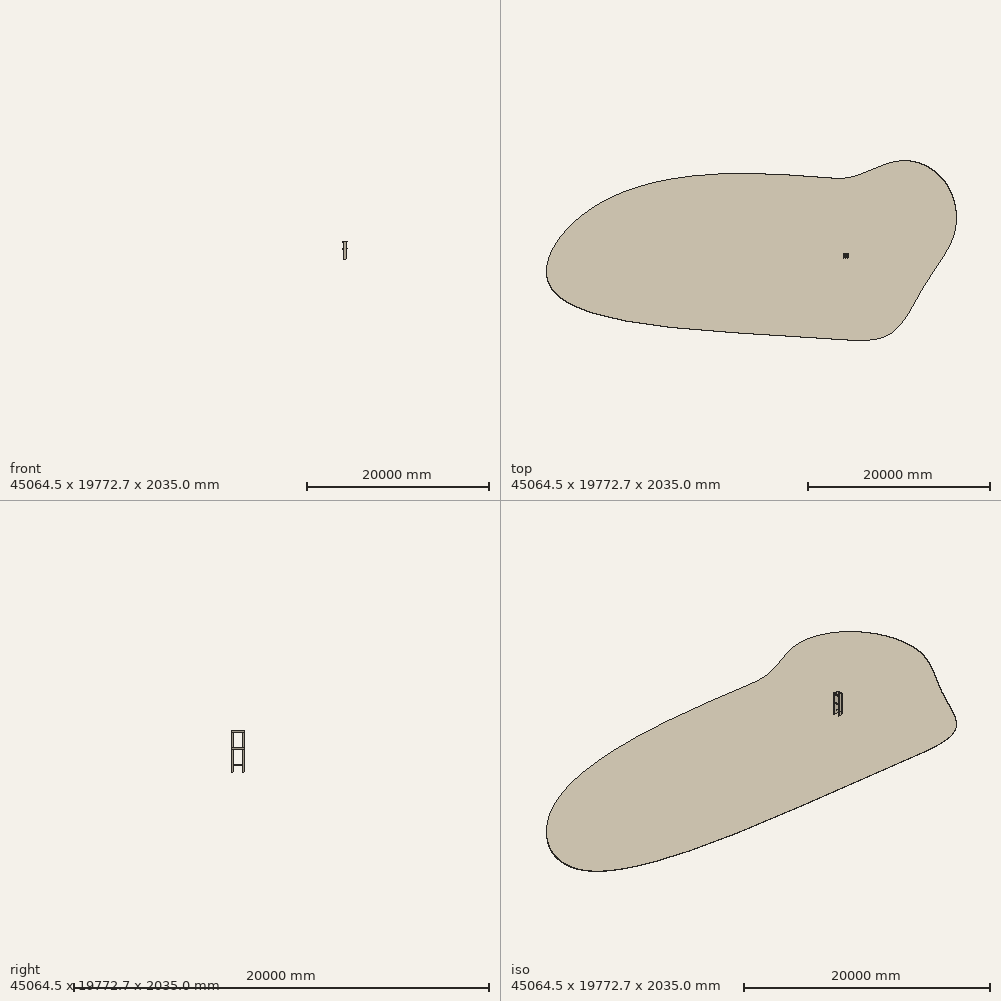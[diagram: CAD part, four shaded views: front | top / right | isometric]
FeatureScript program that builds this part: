
annotation { "Feature Type Name" : "Feature", "Feature Type Description" : "" }
export const myFeature = defineFeature(function(context is Context, id is Id, definition is map)
    precondition{}
    {
        {
            var Q0;
            Q0=qCreatedBy(makeId("Top.planeOp"),FACE);
            var sketch = newSketch(context, id + "F0", { "sketchPlane" : qUnion([Q0])});
            skLineSegment(sketch, "E0", {"start": v(-200, -312.5) * mm, "end": v(-200, -202.5) * mm});
            skLineSegment(sketch, "E1", {"start": v(-200, -202.5) * mm, "end": v(200, -202.5) * mm});
            skLineSegment(sketch, "E2", {"start": v(200, -202.5) * mm, "end": v(200, -312.5) * mm});
            skLineSegment(sketch, "E3", {"start": v(200, -312.5) * mm, "end": v(185, -312.5) * mm});
            skLineSegment(sketch, "E4", {"start": v(185, -312.5) * mm, "end": v(185, -217.5) * mm});
            skLineSegment(sketch, "E5", {"start": v(185, -217.5) * mm, "end": v(-185, -217.5) * mm});
            skLineSegment(sketch, "E6", {"start": v(-185, -217.5) * mm, "end": v(-185, -312.5) * mm});
            skLineSegment(sketch, "E7", {"start": v(-185, -312.5) * mm, "end": v(-200, -312.5) * mm});
            skLineSegment(sketch, "E8.MirrorCS", {"start": v(-200, 312.5) * mm, "end": v(-200, 202.5) * mm});
            skLineSegment(sketch, "E9.MirrorCS", {"start": v(-200, 202.5) * mm, "end": v(200, 202.5) * mm});
            skLineSegment(sketch, "E10.MirrorCS", {"start": v(185, 217.5) * mm, "end": v(-185, 217.5) * mm});
            skLineSegment(sketch, "E11.MirrorCS", {"start": v(185, 312.5) * mm, "end": v(185, 217.5) * mm});
            skLineSegment(sketch, "E12.MirrorCS", {"start": v(-185, 217.5) * mm, "end": v(-185, 312.5) * mm});
            skLineSegment(sketch, "E13.MirrorCS", {"start": v(200, 202.5) * mm, "end": v(200, 312.5) * mm});
            skLineSegment(sketch, "E14.MirrorCS", {"start": v(-185, 312.5) * mm, "end": v(-200, 312.5) * mm});
            skLineSegment(sketch, "E15.MirrorCS", {"start": v(200, 312.5) * mm, "end": v(185, 312.5) * mm});
            skSolve(sketch);
        }
        {
            var Q0;
            Q0 = qSketchRegion(id + "F0", true);
            extrude(context, id + "F1", {"entities" : qUnion([Q0]), "depth" : 2010 * mm, "offsetDistance" : 25 * mm});
        }
        {
            var Q0;
            Q0=makeQuery(id+"F1.opExtrude","SWEPT_FACE",FACE,{"disambiguationData":[OSD([sQuery(id+"F0.wireOp",EDGE,"E5")])]});
            var sketch = newSketch(context, id + "F2", { "sketchPlane" : qUnion([Q0])});
            skCircle(sketch, "E16", {"center": v(0, 355) * mm, "radius": 19 * mm});
            skSolve(sketch);
        }
        {
            var Q0;
            Q0=makeQuery(id+"F2.imprint","IMPRINT",FACE,{"disambiguationData":[TD([[makeQuery(id+"F2.imprint","IMPRINT",EDGE,{"derivedFrom":sQuery(id+"F2.wireOp",EDGE,"E16")}),1.0]])]});
            extrude(context, id + "F3", {"entities" : qUnion([Q0]), "operationType" : NewBodyOperationType.REMOVE, "endBound" : BoundingType.THROUGH_ALL, "oppositeDirection" : true, "depth" : 25 * mm, "offsetDistance" : 25 * mm});
        }
        {
            var Q0;
            Q0=qCreatedBy(makeId("Right.planeOp"),FACE);
            var sketch = newSketch(context, id + "F4", { "sketchPlane" : qUnion([Q0])});
            skCircle(sketch, "E17", {"center": v(-257.5, 1098) * mm, "radius": 7.5 * mm});
            skCircle(sketch, "E18", {"center": v(257.5, 1098) * mm, "radius": 7.5 * mm});
            skCircle(sketch, "E19", {"center": v(-257.5, 1978) * mm, "radius": 7.5 * mm});
            skCircle(sketch, "E20", {"center": v(257.5, 1978) * mm, "radius": 7.5 * mm});
            skCircle(sketch, "E21", {"center": v(257.5, 1937) * mm, "radius": 7.5 * mm});
            skCircle(sketch, "E22", {"center": v(-257.5, 1937) * mm, "radius": 7.5 * mm});
            skCircle(sketch, "E23", {"center": v(257.5, 1158) * mm, "radius": 7.5 * mm});
            skCircle(sketch, "E24", {"center": v(-257.5, 1158) * mm, "radius": 7.5 * mm});
            skSolve(sketch);
        }
        {
            var Q0;
            Q0 = qSketchRegion(id + "F4", true);
            extrude(context, id + "F5", {"entities" : qUnion([Q0]), "operationType" : NewBodyOperationType.REMOVE, "endBound" : BoundingType.THROUGH_ALL, "oppositeDirection" : true, "depth" : 25 * mm, "offsetDistance" : 25 * mm, "hasSecondDirection" : true, "secondDirectionBound" : SecondDirectionBoundingType.THROUGH_ALL, "secondDirectionOppositeDirection" : false, "secondDirectionDepth" : 25 * mm});
        }
        {
            var Q0;
            Q0=qCreatedBy(makeId("Top.planeOp"),FACE);
            var sketch = newSketch(context, id + "F6", { "sketchPlane" : qUnion([Q0])});
            skFitSpline(sketch, "E25", {"points": [v(-26060.01, 6307.68) * mm, v(-4444.75, 8762.1) * mm, v(1029.42, 8782.8) * mm, v(6125.61, 10472.14) * mm, v(10723.74, 8341.28) * mm, v(11981.11, 2728.24) * mm, v(8613.99, -3299.12) * mm, v(5082.12, -8449.76) * mm, v(-4741.28, -8891.89) * mm, v(-32336.68, -3635.44) * mm, v(-26060.01, 6307.68) * mm]});
            skSolve(sketch);
        }
        {
            var Q0;
            Q0=makeQuery(id+"F6.imprint","IMPRINT",FACE,{"disambiguationData":[TD([[makeQuery(id+"F6.imprint","IMPRINT",EDGE,{"derivedFrom":sQuery(id+"F6.wireOp",EDGE,"E25")}),-1.0]])]});
            extrude(context, id + "F7", {"entities" : qUnion([Q0]), "oppositeDirection" : true, "depth" : 25 * mm, "offsetDistance" : 25 * mm});
        }
        {
            var Q0;
            Q0=makeQuery(id+"F1.opExtrude","SWEPT_FACE",FACE,{"disambiguationData":[OSD([sQuery(id+"F0.wireOp",EDGE,"E0")])]});
            var sketch = newSketch(context, id + "F8", { "sketchPlane" : qUnion([Q0])});
            skLineSegment(sketch, "E26.bottom", {"start": v(-300, 1178) * mm, "end": v(300, 1178) * mm});
            skLineSegment(sketch, "E26.top", {"start": v(-300, 1078) * mm, "end": v(300, 1078) * mm});
            skLineSegment(sketch, "E26.left", {"start": v(-300, 1178) * mm, "end": v(-300, 1078) * mm});
            skLineSegment(sketch, "E26.right", {"start": v(300, 1178) * mm, "end": v(300, 1078) * mm});
            skLineSegment(sketch, "E27", {"start": v(-300, 1128) * mm, "end": v(300, 1128) * mm});
            skLineSegment(sketch, "E28.bottom", {"start": v(-300, 2007.5) * mm, "end": v(300, 2007.5) * mm});
            skLineSegment(sketch, "E28.top", {"start": v(-300, 1907.5) * mm, "end": v(300, 1907.5) * mm});
            skLineSegment(sketch, "E28.left", {"start": v(-300, 2007.5) * mm, "end": v(-300, 1907.5) * mm});
            skLineSegment(sketch, "E28.right", {"start": v(300, 2007.5) * mm, "end": v(300, 1907.5) * mm});
            skLineSegment(sketch, "E29", {"start": v(-300, 1957.5) * mm, "end": v(300, 1957.5) * mm});
            skCircle(sketch, "E30.0", {"center": v(-257.5, 1978) * mm, "radius": 7.5 * mm});
            skCircle(sketch, "E31.0", {"center": v(-257.5, 1937) * mm, "radius": 7.5 * mm});
            skCircle(sketch, "E32.0", {"center": v(257.5, 1978) * mm, "radius": 7.5 * mm});
            skCircle(sketch, "E33.0", {"center": v(257.5, 1937) * mm, "radius": 7.5 * mm});
            skCircle(sketch, "E34.0", {"center": v(257.5, 1158) * mm, "radius": 7.5 * mm});
            skCircle(sketch, "E35.0", {"center": v(257.5, 1098) * mm, "radius": 7.5 * mm});
            skCircle(sketch, "E36.0", {"center": v(-257.5, 1098) * mm, "radius": 7.5 * mm});
            skCircle(sketch, "E37.0", {"center": v(-257.5, 1158) * mm, "radius": 7.5 * mm});
            skSolve(sketch);
        }
        {
            var Q0;
            {var subQ6=sQuery(id+"F8.wireOp",EDGE,"E28.bottom");Q0=makeQuery(id+"F8.imprint","IMPRINT",FACE,{"disambiguationData":[TD([[makeQuery(id+"F8.imprint","IMPRINT",EDGE,{"derivedFrom":subQ6}),-1.0]])]});}
            var Q1;
            Q1=makeQuery(id+"F8.imprint","IMPRINT",FACE,{"disambiguationData":[TD([[makeQuery(id+"F8.imprint","IMPRINT",EDGE,{"derivedFrom":sQuery(id+"F8.wireOp",EDGE,"E31.0")}),-1.0]])]});
            var Q2;
            Q2=makeQuery(id+"F8.imprint","IMPRINT",FACE,{"disambiguationData":[TD([[makeQuery(id+"F8.imprint","IMPRINT",EDGE,{"derivedFrom":sQuery(id+"F8.wireOp",EDGE,"E37.0")}),-1.0]])]});
            var Q3;
            Q3=makeQuery(id+"F8.imprint","IMPRINT",FACE,{"disambiguationData":[TD([[makeQuery(id+"F8.imprint","IMPRINT",EDGE,{"derivedFrom":sQuery(id+"F8.wireOp",EDGE,"E36.0")}),-1.0]])]});
            var Q4;
            Q4=makeQuery(id+"F8.imprint","IMPRINT",FACE,{"disambiguationData":[TD([[makeQuery(id+"F8.imprint","IMPRINT",EDGE,{"derivedFrom":sQuery(id+"F8.wireOp",EDGE,"E34.0")}),-1.0]])]});
            var Q5;
            Q5=makeQuery(id+"F8.imprint","IMPRINT",FACE,{"disambiguationData":[TD([[makeQuery(id+"F8.imprint","IMPRINT",EDGE,{"derivedFrom":sQuery(id+"F8.wireOp",EDGE,"E35.0")}),-1.0]])]});
            var Q6;
            Q6=makeQuery(id+"F8.imprint","IMPRINT",FACE,{"disambiguationData":[TD([[makeQuery(id+"F8.imprint","IMPRINT",EDGE,{"derivedFrom":sQuery(id+"F8.wireOp",EDGE,"E32.0")}),-1.0]])]});
            var Q7;
            Q7=makeQuery(id+"F8.imprint","IMPRINT",FACE,{"disambiguationData":[TD([[makeQuery(id+"F8.imprint","IMPRINT",EDGE,{"derivedFrom":sQuery(id+"F8.wireOp",EDGE,"E33.0")}),-1.0]])]});
            extrude(context, id + "F9", {"entities" : qUnion([Q0, Q1, Q2, Q3, Q4, Q5, Q6, Q7]), "depth" : 25 * mm, "offsetDistance" : 25 * mm});
        }
        {
            var Q0;
            Q0=makeQuery(id+"F9.opExtrude","SWEPT_BODY",BODY,{"disambiguationData":[OSD([sQuery(id+"F8.wireOp",EDGE,"E28.bottom"),sQuery(id+"F8.wireOp",EDGE,"E28.top"),sQuery(id+"F8.wireOp",EDGE,"E28.left"),sQuery(id+"F8.wireOp",EDGE,"E28.right"),sQuery(id+"F8.wireOp",EDGE,"E30.0"),sQuery(id+"F8.wireOp",EDGE,"E31.0"),sQuery(id+"F8.wireOp",EDGE,"E32.0"),sQuery(id+"F8.wireOp",EDGE,"E33.0")])]});
            var Q1;
            Q1=makeQuery(id+"F9.opExtrude","SWEPT_BODY",BODY,{"disambiguationData":[OSD([sQuery(id+"F8.wireOp",EDGE,"E26.bottom"),sQuery(id+"F8.wireOp",EDGE,"E26.top"),sQuery(id+"F8.wireOp",EDGE,"E26.left"),sQuery(id+"F8.wireOp",EDGE,"E26.right"),sQuery(id+"F8.wireOp",EDGE,"E34.0"),sQuery(id+"F8.wireOp",EDGE,"E35.0"),sQuery(id+"F8.wireOp",EDGE,"E36.0"),sQuery(id+"F8.wireOp",EDGE,"E37.0")])]});
            var Q2;
            Q2=qCreatedBy(makeId("Right.planeOp"),FACE);
            mirror(context, id + "F10", {"entities" : qUnion([Q0, Q1]), "mirrorPlane" : qUnion([Q2])});
        }
        {
            var Q0;
            Q0=qCreatedBy(makeId("Right.planeOp"),FACE);
            var sketch = newSketch(context, id + "F11", { "sketchPlane" : qUnion([Q0])});
            skLineSegment(sketch, "E38", {"start": v(-217.5, 336) * mm, "end": v(-202.5, 336) * mm});
            skLineSegment(sketch, "E39", {"start": v(-202.5, 374) * mm, "end": v(-217.5, 374) * mm});
            skLineSegment(sketch, "E40.bottom", {"start": v(262.5, 372.5) * mm, "end": v(-217.5, 372.5) * mm});
            skLineSegment(sketch, "E40.top", {"start": v(262.5, 337.5) * mm, "end": v(-217.5, 337.5) * mm});
            skLineSegment(sketch, "E40.left", {"start": v(262.5, 372.5) * mm, "end": v(262.5, 337.5) * mm});
            skLineSegment(sketch, "E40.right", {"start": v(-217.5, 372.5) * mm, "end": v(-217.5, 337.5) * mm});
            skLineSegment(sketch, "E41", {"start": v(-217.5, 355) * mm, "end": v(262.5, 355) * mm});
            skLineSegment(sketch, "E42.bottom", {"start": v(-217.5, 377.5) * mm, "end": v(-227.5, 377.5) * mm});
            skLineSegment(sketch, "E42.top", {"start": v(-217.5, 332.5) * mm, "end": v(-227.5, 332.5) * mm});
            skLineSegment(sketch, "E42.left", {"start": v(-217.5, 377.5) * mm, "end": v(-217.5, 332.5) * mm});
            skLineSegment(sketch, "E42.right", {"start": v(-227.5, 377.5) * mm, "end": v(-227.5, 332.5) * mm});
            skLineSegment(sketch, "E43", {"start": v(-217.5, 355) * mm, "end": v(-227.5, 355) * mm});
            skSolve(sketch);
        }
        {
            var Q0;
            {var subQ0=sQuery(id+"F11.wireOp",EDGE,"E40.bottom");Q0=makeQuery(id+"F11.imprint","IMPRINT",FACE,{"disambiguationData":[TD([[makeQuery(id+"F11.imprint","IMPRINT",EDGE,{"derivedFrom":subQ0}),1.0]])]});}
            var Q1;
            {var subQ4=sQuery(id+"F11.wireOp",EDGE,"E42.bottom");Q1=makeQuery(id+"F11.imprint","IMPRINT",FACE,{"disambiguationData":[TD([[makeQuery(id+"F11.imprint","IMPRINT",EDGE,{"derivedFrom":subQ4}),1.0]])]});}
            var Q2;
            Q2=sQuery(id+"F11.wireOp",EDGE,"E41");
            revolve(context, id + "F12", {"surfaceOperationType" : NewSurfaceOperationType.NEW, "entities" : qUnion([Q0, Q1]), "axis" : qUnion([Q2]), "revolveType" : RevolveType.FULL});
        }
    });
